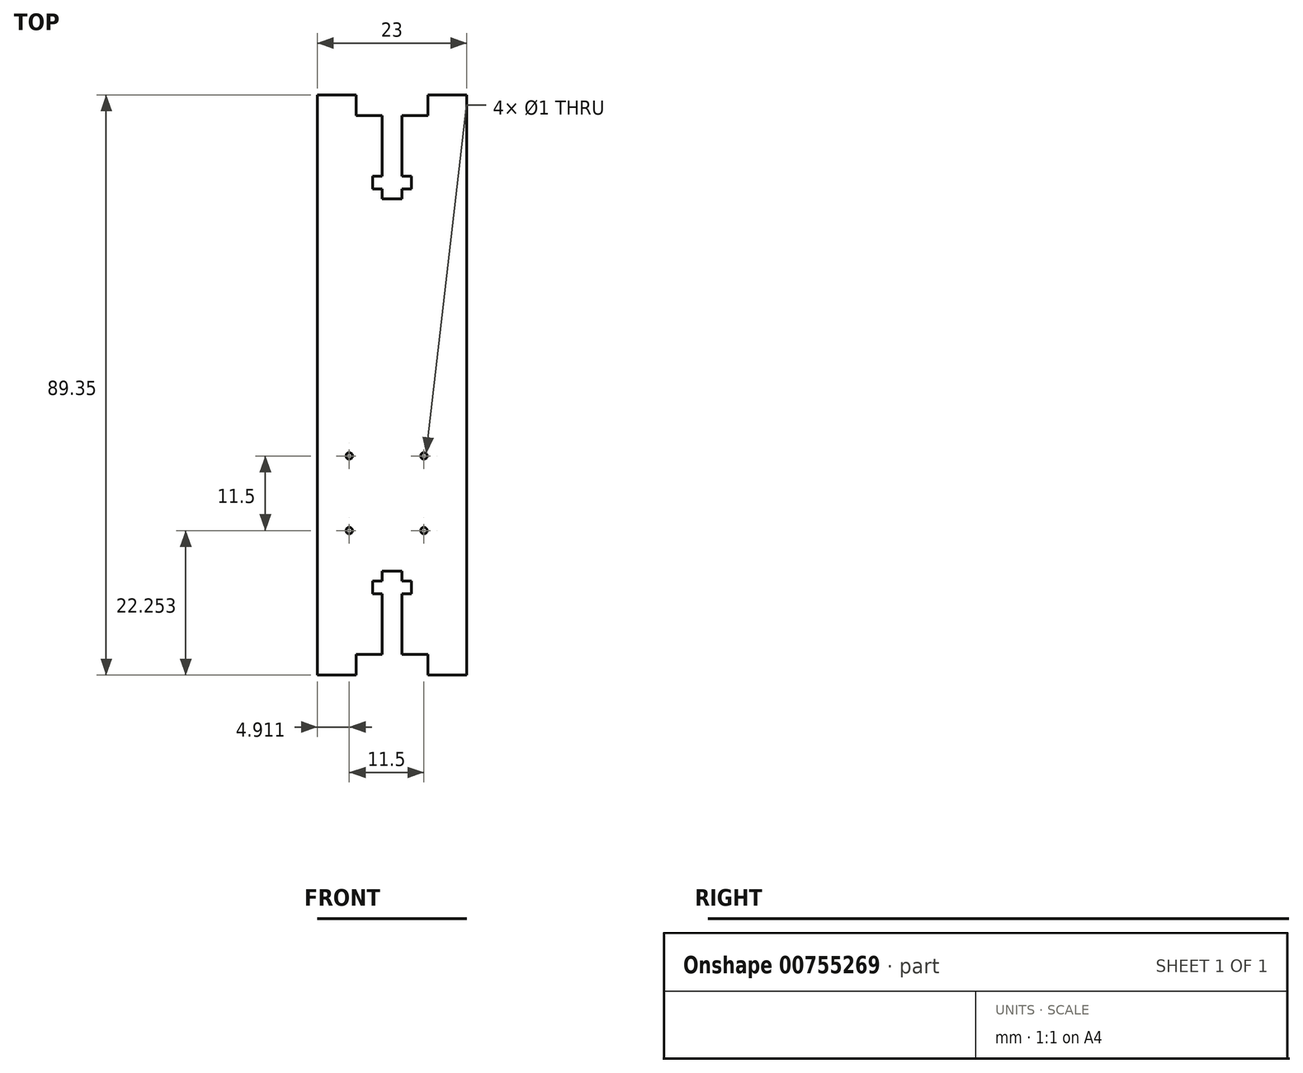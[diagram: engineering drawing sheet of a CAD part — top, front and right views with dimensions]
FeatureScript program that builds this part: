
annotation { "Feature Type Name" : "Feature", "Feature Type Description" : "" }
export const myFeature = defineFeature(function(context is Context, id is Id, definition is map)
    precondition{}
    {
        {
            var Q0;
            Q0=qCreatedBy(makeId("Top.planeOp"),FACE);
            var sketch = newSketch(context, id + "F0", { "sketchPlane" : qUnion([Q0])});
            skLineSegment(sketch, "E0.top", {"start": v(-37.34, 49.07) * mm, "end": v(-34.34, 49.07) * mm});
            skLineSegment(sketch, "E0.left", {"start": v(-37.34, 61.9) * mm, "end": v(-37.34, 52.57) * mm});
            skLineSegment(sketch, "E0.right", {"start": v(-34.34, 61.9) * mm, "end": v(-34.34, 52.57) * mm});
            skPoint(sketch, "E0.middle", {"position": v(-35.84, 57.07) * mm});
            skLineSegment(sketch, "E1.bottom", {"start": v(-38.84, 52.57) * mm, "end": v(-37.34, 52.57) * mm});
            skLineSegment(sketch, "E1.top", {"start": v(-38.84, 50.57) * mm, "end": v(-37.34, 50.57) * mm});
            skLineSegment(sketch, "E1.left", {"start": v(-38.84, 52.57) * mm, "end": v(-38.84, 50.57) * mm});
            skLineSegment(sketch, "E1.right", {"start": v(-32.84, 52.57) * mm, "end": v(-32.84, 50.57) * mm});
            skPoint(sketch, "E1.middle", {"position": v(-35.84, 51.57) * mm});
            skLineSegment(sketch, "E2.bottom", {"start": v(-30.34, 65.07) * mm, "end": v(-24.34, 65.07) * mm});
            skLineSegment(sketch, "E2.left", {"start": v(-30.34, 65.07) * mm, "end": v(-30.34, 61.9) * mm});
            skLineSegment(sketch, "E2.right", {"start": v(-24.34, 65.07) * mm, "end": v(-24.34, 61.9) * mm});
            skLineSegment(sketch, "E3.MirrorCS", {"start": v(-41.34, 65.07) * mm, "end": v(-41.34, 61.9) * mm});
            skLineSegment(sketch, "E4.MirrorCS", {"start": v(-41.34, 65.07) * mm, "end": v(-47.34, 65.07) * mm});
            skLineSegment(sketch, "E5.MirrorCS", {"start": v(-47.34, 65.07) * mm, "end": v(-47.34, 61.9) * mm});
            skLineSegment(sketch, "E6", {"start": v(-41.34, 61.9) * mm, "end": v(-37.34, 61.9) * mm});
            skLineSegment(sketch, "E7.bottom", {"start": v(-37.34, -8.28) * mm, "end": v(-34.34, -8.28) * mm});
            skLineSegment(sketch, "E7.left", {"start": v(-37.34, -8.28) * mm, "end": v(-37.34, -9.78) * mm});
            skLineSegment(sketch, "E7.right", {"start": v(-34.34, -8.28) * mm, "end": v(-34.34, -9.78) * mm});
            skPoint(sketch, "E7.middle", {"position": v(-35.84, -16.28) * mm});
            skLineSegment(sketch, "E8.bottom", {"start": v(-38.84, -9.78) * mm, "end": v(-37.34, -9.78) * mm});
            skLineSegment(sketch, "E8.top", {"start": v(-38.84, -11.78) * mm, "end": v(-37.34, -11.78) * mm});
            skLineSegment(sketch, "E8.left", {"start": v(-38.84, -9.78) * mm, "end": v(-38.84, -11.78) * mm});
            skLineSegment(sketch, "E8.right", {"start": v(-32.84, -9.78) * mm, "end": v(-32.84, -11.78) * mm});
            skPoint(sketch, "E8.middle", {"position": v(-35.84, -10.78) * mm});
            skLineSegment(sketch, "E9.bottom", {"start": v(-30.34, -24.28) * mm, "end": v(-24.34, -24.28) * mm});
            skLineSegment(sketch, "E9.left", {"start": v(-30.34, -24.28) * mm, "end": v(-30.34, -21.1) * mm});
            skLineSegment(sketch, "E9.right", {"start": v(-24.34, -24.28) * mm, "end": v(-24.34, -21.1) * mm});
            skLineSegment(sketch, "E10.MirrorCS", {"start": v(-41.34, -24.28) * mm, "end": v(-41.34, -21.1) * mm});
            skLineSegment(sketch, "E11.MirrorCS", {"start": v(-47.34, -24.28) * mm, "end": v(-47.34, -21.1) * mm});
            skLineSegment(sketch, "E12.MirrorCS", {"start": v(-41.34, -24.28) * mm, "end": v(-47.34, -24.28) * mm});
            skLineSegment(sketch, "E13", {"start": v(-47.34, 61.9) * mm, "end": v(-47.34, -21.1) * mm});
            skLineSegment(sketch, "E14", {"start": v(-24.34, 61.9) * mm, "end": v(-24.34, -21.1) * mm});
            skLineSegment(sketch, "E15", {"start": v(-30.34, -21.1) * mm, "end": v(-34.34, -21.1) * mm});
            skCircle(sketch, "E16", {"center": v(-42.43, 9.47) * mm, "radius": 0.5 * mm});
            skCircle(sketch, "E17.MirrorC", {"center": v(-30.93, 9.47) * mm, "radius": 0.5 * mm});
            skCircle(sketch, "E18.MirrorC", {"center": v(-42.43, -2.03) * mm, "radius": 0.5 * mm});
            skCircle(sketch, "E19.MirrorC", {"center": v(-30.93, -2.03) * mm, "radius": 0.5 * mm});
            skPoint(sketch, "E20.MirrorCS.end.orphan", {"position": v(-47.34, 61.9) * mm});
            skPoint(sketch, "E20.MirrorCS.start.orphan", {"position": v(-41.34, 61.9) * mm});
            skPoint(sketch, "E21.orphan", {"position": v(-34.34, 65.07) * mm});
            skPoint(sketch, "E22.orphan", {"position": v(-37.34, 65.07) * mm});
            skLineSegment(sketch, "E23.trimOffspring", {"start": v(-34.34, 61.9) * mm, "end": v(-30.34, 61.9) * mm});
            skLineSegment(sketch, "E24.trimOffspring", {"start": v(-34.34, 52.57) * mm, "end": v(-32.84, 52.57) * mm});
            skLineSegment(sketch, "E25.trimOffspring", {"start": v(-37.34, 50.57) * mm, "end": v(-37.34, 49.07) * mm});
            skLineSegment(sketch, "E26.trimOffspring", {"start": v(-34.34, 50.57) * mm, "end": v(-32.84, 50.57) * mm});
            skLineSegment(sketch, "E27.trimOffspring", {"start": v(-34.34, 50.57) * mm, "end": v(-34.34, 49.07) * mm});
            skPoint(sketch, "E28.end.orphan", {"position": v(-36.68, 9.47) * mm});
            skPoint(sketch, "E29.start.orphan", {"position": v(-42.43, 3.72) * mm});
            skPoint(sketch, "E30.MirrorCS.start.orphan", {"position": v(-41.34, -21.1) * mm});
            skPoint(sketch, "E7.top.end.orphan", {"position": v(-34.34, -24.28) * mm});
            skPoint(sketch, "E7.top.start.orphan", {"position": v(-37.34, -24.28) * mm});
            skLineSegment(sketch, "E31.trimOffspring", {"start": v(-37.34, -21.1) * mm, "end": v(-41.34, -21.1) * mm});
            skLineSegment(sketch, "E32.trimOffspring", {"start": v(-34.34, -11.78) * mm, "end": v(-32.84, -11.78) * mm});
            skLineSegment(sketch, "E33.trimOffspring", {"start": v(-34.34, -11.78) * mm, "end": v(-34.34, -21.1) * mm});
            skLineSegment(sketch, "E34.trimOffspring", {"start": v(-34.34, -9.78) * mm, "end": v(-32.84, -9.78) * mm});
            skLineSegment(sketch, "E35.trimOffspring", {"start": v(-37.34, -11.78) * mm, "end": v(-37.34, -21.1) * mm});
            skSolve(sketch);
        }
        {
            var Q0;
            {var subQ23=sQuery(id+"F0.wireOp",EDGE,"E0.top");Q0=makeQuery(id+"F0.imprint","IMPRINT",FACE,{"disambiguationData":[TD([[makeQuery(id+"F0.imprint","IMPRINT",EDGE,{"derivedFrom":subQ23}),-1.0]])]});}
            var Q1;
            Q1=makeQuery(id+"F0.imprint","IMPRINT",FACE,{"disambiguationData":[TD([[makeQuery(id+"F0.imprint","IMPRINT",EDGE,{"derivedFrom":sQuery(id+"F0.wireOp",EDGE,"E2.bottom")}),-1.0]])]});
            var Q2;
            Q2=makeQuery(id+"F0.imprint","IMPRINT",FACE,{"disambiguationData":[TD([[makeQuery(id+"F0.imprint","IMPRINT",EDGE,{"derivedFrom":sQuery(id+"F0.wireOp",EDGE,"E3.MirrorCS")}),-1.0]])]});
            var Q3;
            Q3=makeQuery(id+"F0.imprint","IMPRINT",FACE,{"disambiguationData":[TD([[makeQuery(id+"F0.imprint","IMPRINT",EDGE,{"derivedFrom":sQuery(id+"F0.wireOp",EDGE,"E10.MirrorCS")}),1.0]])]});
            var Q4;
            Q4=makeQuery(id+"F0.imprint","IMPRINT",FACE,{"disambiguationData":[TD([[makeQuery(id+"F0.imprint","IMPRINT",EDGE,{"derivedFrom":sQuery(id+"F0.wireOp",EDGE,"E9.bottom")}),1.0]])]});
            extrude(context, id + "F1", {"entities" : qUnion([Q0, Q1, Q2, Q3, Q4]), "depth" : 1 / 203.2 * mm, "offsetDistance" : 25 * mm});
        }
    });
